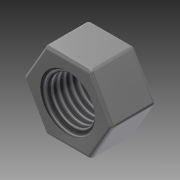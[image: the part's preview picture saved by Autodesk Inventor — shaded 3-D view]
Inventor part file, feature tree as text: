
AUTODESK INVENTOR PART (.ipt)
format: ipt  version: 2021 (Build 250183000, 183)  size: 156,672 bytes
history: native  units: mm
features: thread x3, other x1, extrude x1, fillet x1, chamfer x1, sketch x1
ambient origin geometry x8: Origin, YZ Plane, XZ Plane, XY Plane, X Axis, Y Axis, Z Axis, Center Point
bodies: Body1 (feature_tree)
feature tree (8):
  other  "Sólido1"
  extrude  "Extrusión1"  Depth=7.0mm
  thread  "Rosca1"  [1 undecoded]
  fillet  "Empalme1"  Radius=7.0mm
  chamfer  "Chaflán1"  Distance=7.0mm
  thread  "Rosca2"  [1 undecoded]
  thread  "Rosca3"  [1 undecoded]
  sketch  "Boceto1"  dims[d21=7.0mm d22=7.0mm d23=120.0deg d24=7.0mm d25=7.0mm d26=7.0mm d27=120.0deg d28=7.0mm d29=7.0mm d30=0.0mm d31=10.0mm d32=0.0mm d33=0.5mm d34=0.8mm d35=2.0mm d36=45.0deg d37=10.0mm d38=0.0mm d39=10.0mm d40=0.0mm]
note: 3 required parameter values undecoded (feature->parameter linkage not recoverable at this tier; creation-order binding heuristic only, values carry confidence <= 0.55)
